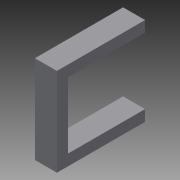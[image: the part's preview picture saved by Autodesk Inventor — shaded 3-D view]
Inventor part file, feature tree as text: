
AUTODESK INVENTOR PART (.ipt)
format: ipt  version: 2014 (Build 180170000, 170)  size: 75,264 bytes
history: native  units: in
note: dims shown in document units (in); Inventor stores cm internally (conversion verified against a paired STEP export)
features: extrude x1, sketch x1
ambient origin geometry x8: Origin, YZ Plane, XZ Plane, XY Plane, X Axis, Y Axis, Z Axis, Center Point
bodies: Solid1 (feature_tree)
feature tree (2):
  extrude  "Extrusion1"  Depth=0.25in
  sketch  "Sketch1"  dims[d0=2.0in d1=0.25in d2=1.75in d3=1.5in d4=1.75in d5=0.25in d6=0.5in d7=0.0in]
